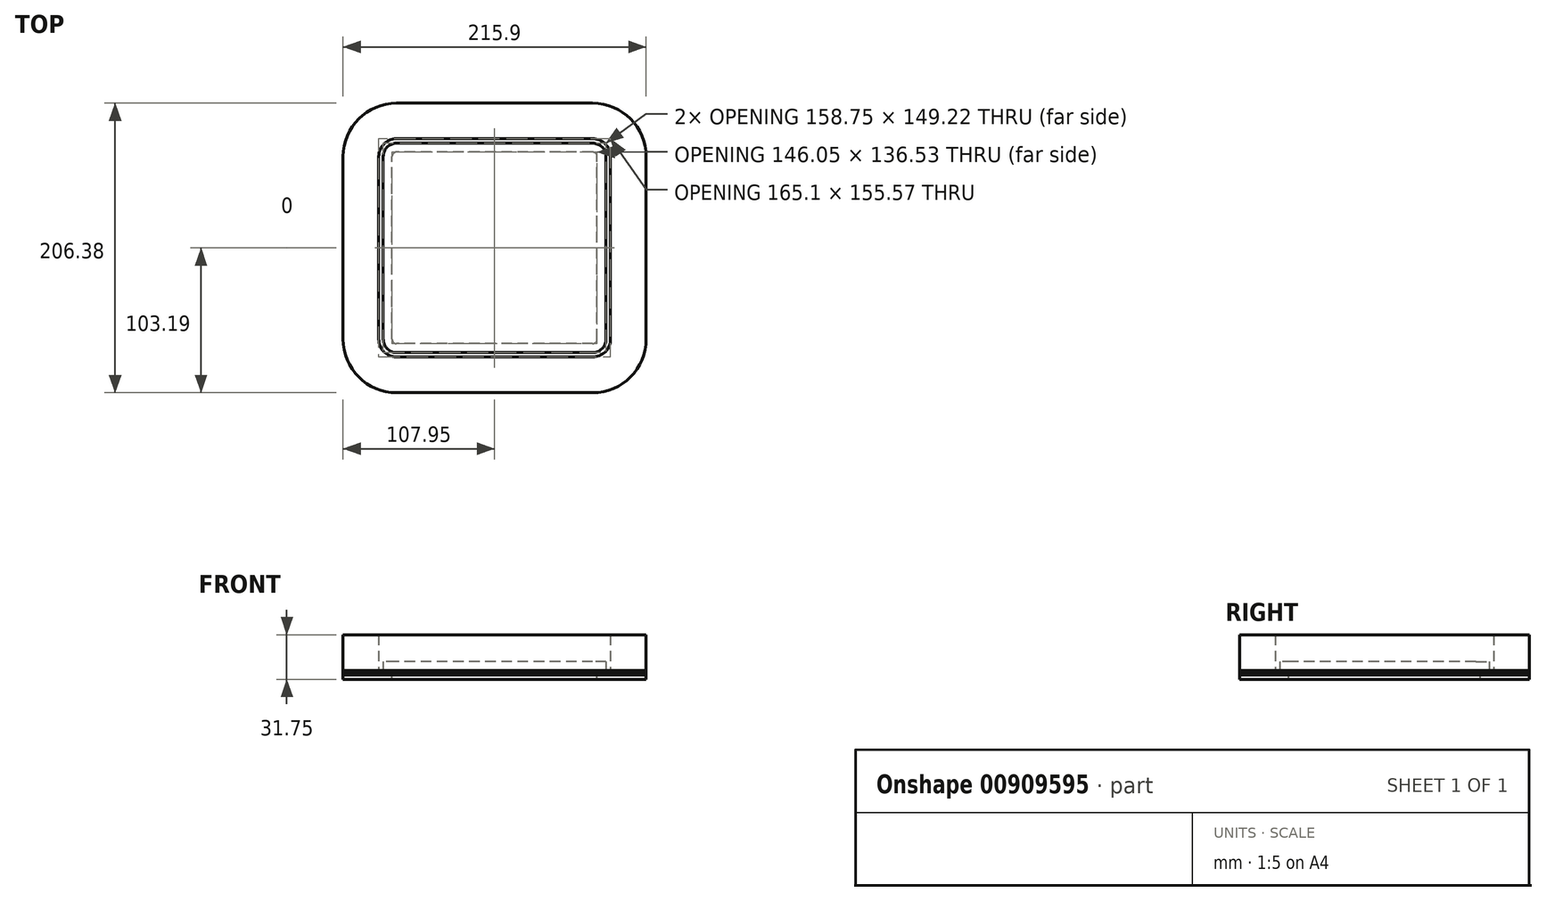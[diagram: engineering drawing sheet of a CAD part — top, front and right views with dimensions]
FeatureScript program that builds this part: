
annotation { "Feature Type Name" : "Feature", "Feature Type Description" : "" }
export const myFeature = defineFeature(function(context is Context, id is Id, definition is map)
    precondition{}
    {
        {
            var Q0;
            Q0=qCreatedBy(makeId("Top.planeOp"),FACE);
            var sketch = newSketch(context, id + "F0", { "sketchPlane" : qUnion([Q0])});
            skLineSegment(sketch, "E0.bottom", {"start": v(69.85, 77.79) * mm, "end": v(-69.85, 77.79) * mm});
            skLineSegment(sketch, "E0.top", {"start": v(69.85, -77.79) * mm, "end": v(-69.85, -77.79) * mm});
            skLineSegment(sketch, "E0.left", {"start": v(82.55, 65.09) * mm, "end": v(82.55, -65.09) * mm});
            skLineSegment(sketch, "E0.right", {"start": v(-82.55, 65.09) * mm, "end": v(-82.55, -65.09) * mm});
            skPoint(sketch, "E0.middle", {"position": v(0, 0) * mm});
            skPoint(sketch, "E1.visualSharp", {"position": v(-82.55, 77.79) * mm});
            skArc(sketch, "E1.filletArc", {"start": v(-69.85, 77.79) * mm, "mid": v(-78.83, 74.07) * mm, "end": v(-82.55, 65.09) * mm});
            skPoint(sketch, "E2.visualSharp", {"position": v(82.55, 77.79) * mm});
            skArc(sketch, "E2.filletArc", {"start": v(82.55, 65.09) * mm, "mid": v(78.83, 74.07) * mm, "end": v(69.85, 77.79) * mm});
            skPoint(sketch, "E3.visualSharp", {"position": v(82.55, -77.79) * mm});
            skArc(sketch, "E3.filletArc", {"start": v(69.85, -77.79) * mm, "mid": v(78.83, -74.07) * mm, "end": v(82.55, -65.09) * mm});
            skPoint(sketch, "E4.visualSharp", {"position": v(-82.55, -77.79) * mm});
            skArc(sketch, "E4.filletArc", {"start": v(-82.55, -65.09) * mm, "mid": v(-78.83, -74.07) * mm, "end": v(-69.85, -77.79) * mm});
            skLineSegment(sketch, "E5.0", {"start": v(-107.95, 65.09) * mm, "end": v(-107.95, -65.09) * mm});
            skArc(sketch, "E5.1", {"start": v(-69.85, 103.19) * mm, "mid": v(-96.8, 92.03) * mm, "end": v(-107.95, 65.09) * mm});
            skArc(sketch, "E5.2", {"start": v(-107.95, -65.09) * mm, "mid": v(-96.8, -92.03) * mm, "end": v(-69.85, -103.19) * mm});
            skLineSegment(sketch, "E5.3", {"start": v(69.85, 103.19) * mm, "end": v(-69.85, 103.19) * mm});
            skLineSegment(sketch, "E5.4", {"start": v(69.85, -103.19) * mm, "end": v(-69.85, -103.19) * mm});
            skArc(sketch, "E5.5", {"start": v(69.85, -103.19) * mm, "mid": v(96.8, -92.03) * mm, "end": v(107.95, -65.09) * mm});
            skLineSegment(sketch, "E5.6", {"start": v(107.95, 65.09) * mm, "end": v(107.95, -65.09) * mm});
            skArc(sketch, "E5.7", {"start": v(107.95, 65.09) * mm, "mid": v(96.8, 92.03) * mm, "end": v(69.85, 103.19) * mm});
            skArc(sketch, "E6.0", {"start": v(79.38, 65.09) * mm, "mid": v(76.59, 71.82) * mm, "end": v(69.85, 74.61) * mm});
            skLineSegment(sketch, "E6.1", {"start": v(69.85, 74.61) * mm, "end": v(-69.85, 74.61) * mm});
            skLineSegment(sketch, "E6.2", {"start": v(79.38, 65.09) * mm, "end": v(79.38, -65.09) * mm});
            skArc(sketch, "E6.3", {"start": v(-69.85, 74.61) * mm, "mid": v(-76.59, 71.82) * mm, "end": v(-79.38, 65.09) * mm});
            skArc(sketch, "E6.4", {"start": v(69.85, -74.61) * mm, "mid": v(76.59, -71.82) * mm, "end": v(79.38, -65.09) * mm});
            skLineSegment(sketch, "E6.5", {"start": v(69.85, -74.61) * mm, "end": v(-69.85, -74.61) * mm});
            skArc(sketch, "E6.6", {"start": v(-79.38, -65.09) * mm, "mid": v(-76.59, -71.82) * mm, "end": v(-69.85, -74.61) * mm});
            skLineSegment(sketch, "E6.7", {"start": v(-79.38, 65.09) * mm, "end": v(-79.38, -65.09) * mm});
            skArc(sketch, "E7.0", {"start": v(69.85, -68.26) * mm, "mid": v(72.1, -67.33) * mm, "end": v(73.03, -65.09) * mm});
            skLineSegment(sketch, "E7.1", {"start": v(73.03, 65.09) * mm, "end": v(73.03, -65.09) * mm});
            skLineSegment(sketch, "E7.2", {"start": v(69.85, -68.26) * mm, "end": v(-69.85, -68.26) * mm});
            skArc(sketch, "E7.3", {"start": v(73.03, 65.09) * mm, "mid": v(72.1, 67.33) * mm, "end": v(69.85, 68.26) * mm});
            skArc(sketch, "E7.4", {"start": v(-73.03, -65.09) * mm, "mid": v(-72.1, -67.33) * mm, "end": v(-69.85, -68.26) * mm});
            skLineSegment(sketch, "E7.5", {"start": v(-73.02, 65.09) * mm, "end": v(-73.03, -65.09) * mm});
            skArc(sketch, "E7.6", {"start": v(-69.85, 68.26) * mm, "mid": v(-72.1, 67.33) * mm, "end": v(-73.02, 65.09) * mm});
            skLineSegment(sketch, "E7.7", {"start": v(69.85, 68.26) * mm, "end": v(-69.85, 68.26) * mm});
            skSolve(sketch);
        }
        {
            var Q0;
            Q0=makeQuery(id+"F0.imprint","IMPRINT",FACE,{"disambiguationData":[TD([[makeQuery(id+"F0.imprint","IMPRINT",EDGE,{"derivedFrom":sQuery(id+"F0.wireOp",EDGE,"E0.bottom")}),-1.0]])]});
            extrude(context, id + "F1", {"entities" : qUnion([Q0]), "depth" : 25.4 * mm, "offsetDistance" : 25.4 * mm});
        }
        {
            var Q0;
            Q0=makeQuery(id+"F0.imprint","IMPRINT",FACE,{"disambiguationData":[TD([[makeQuery(id+"F0.imprint","IMPRINT",EDGE,{"derivedFrom":sQuery(id+"F0.wireOp",EDGE,"E6.0")}),1.0]])]});
            var Q1;
            Q1=makeQuery(id+"F0.imprint","IMPRINT",FACE,{"disambiguationData":[TD([[makeQuery(id+"F0.imprint","IMPRINT",EDGE,{"derivedFrom":sQuery(id+"F0.wireOp",EDGE,"E7.0")}),1.0]])]});
            extrude(context, id + "F2", {"entities" : qUnion([Q0, Q1]), "depth" : 6.35 * mm, "offsetDistance" : 25.4 * mm});
        }
        {
            var Q0;
            Q0=makeQuery(id+"F0.imprint","IMPRINT",FACE,{"disambiguationData":[TD([[makeQuery(id+"F0.imprint","IMPRINT",EDGE,{"derivedFrom":sQuery(id+"F0.wireOp",EDGE,"E0.bottom")}),-1.0]])]});
            var Q1;
            Q1=makeQuery(id+"F0.imprint","IMPRINT",FACE,{"disambiguationData":[TD([[makeQuery(id+"F0.imprint","IMPRINT",EDGE,{"derivedFrom":sQuery(id+"F0.wireOp",EDGE,"E0.bottom")}),1.0]])]});
            extrude(context, id + "F3", {"entities" : qUnion([Q0, Q1]), "oppositeDirection" : true, "depth" : 1.59 * mm, "offsetDistance" : 25.4 * mm});
        }
        {
            var Q0;
            Q0=makeQuery(id+"F3.opExtrude","CAP_FACE",FACE,{"disambiguationData":[OSD([sQuery(id+"F0.wireOp",EDGE,"E5.0"),sQuery(id+"F0.wireOp",EDGE,"E5.1"),sQuery(id+"F0.wireOp",EDGE,"E5.2"),sQuery(id+"F0.wireOp",EDGE,"E5.3"),sQuery(id+"F0.wireOp",EDGE,"E5.4"),sQuery(id+"F0.wireOp",EDGE,"E5.5"),sQuery(id+"F0.wireOp",EDGE,"E5.6"),sQuery(id+"F0.wireOp",EDGE,"E5.7"),sQuery(id+"F0.wireOp",EDGE,"E7.0"),sQuery(id+"F0.wireOp",EDGE,"E7.1"),sQuery(id+"F0.wireOp",EDGE,"E7.2"),sQuery(id+"F0.wireOp",EDGE,"E7.3"),sQuery(id+"F0.wireOp",EDGE,"E7.4"),sQuery(id+"F0.wireOp",EDGE,"E7.5"),sQuery(id+"F0.wireOp",EDGE,"E7.6"),sQuery(id+"F0.wireOp",EDGE,"E7.7")])],"isStart":false});
            extrude(context, id + "F4", {"entities" : qUnion([Q0]), "depth" : 1.59 * mm, "offsetDistance" : 25.4 * mm});
        }
        {
            var Q0;
            Q0=makeQuery(id+"F4.opExtrude","CAP_FACE",FACE,{"disambiguationData":[OSD([sQuery(id+"F0.wireOp",EDGE,"E5.0"),sQuery(id+"F0.wireOp",EDGE,"E5.1"),sQuery(id+"F0.wireOp",EDGE,"E5.2"),sQuery(id+"F0.wireOp",EDGE,"E5.3"),sQuery(id+"F0.wireOp",EDGE,"E5.4"),sQuery(id+"F0.wireOp",EDGE,"E5.5"),sQuery(id+"F0.wireOp",EDGE,"E5.6"),sQuery(id+"F0.wireOp",EDGE,"E5.7"),sQuery(id+"F0.wireOp",EDGE,"E6.0"),sQuery(id+"F0.wireOp",EDGE,"E6.1"),sQuery(id+"F0.wireOp",EDGE,"E6.2"),sQuery(id+"F0.wireOp",EDGE,"E6.3"),sQuery(id+"F0.wireOp",EDGE,"E6.4"),sQuery(id+"F0.wireOp",EDGE,"E6.5"),sQuery(id+"F0.wireOp",EDGE,"E6.6"),sQuery(id+"F0.wireOp",EDGE,"E6.7")])],"isStart":false});
            var sketch = newSketch(context, id + "F5", { "sketchPlane" : qUnion([Q0])});
            skLineSegment(sketch, "E8.bottom", {"start": v(69.85, 77.79) * mm, "end": v(-69.85, 77.79) * mm});
            skLineSegment(sketch, "E8.top", {"start": v(69.85, -77.79) * mm, "end": v(-69.85, -77.79) * mm});
            skLineSegment(sketch, "E8.left", {"start": v(82.55, 65.09) * mm, "end": v(82.55, -65.09) * mm});
            skLineSegment(sketch, "E8.right", {"start": v(-82.55, 65.09) * mm, "end": v(-82.55, -65.09) * mm});
            skPoint(sketch, "E8.middle", {"position": v(0, 0) * mm});
            skPoint(sketch, "E9.visualSharp", {"position": v(-82.55, 77.79) * mm});
            skArc(sketch, "E9.filletArc", {"start": v(-69.85, 77.79) * mm, "mid": v(-78.83, 74.07) * mm, "end": v(-82.55, 65.09) * mm});
            skPoint(sketch, "E10.visualSharp", {"position": v(82.55, 77.79) * mm});
            skArc(sketch, "E10.filletArc", {"start": v(82.55, 65.09) * mm, "mid": v(78.83, 74.07) * mm, "end": v(69.85, 77.79) * mm});
            skPoint(sketch, "E11.visualSharp", {"position": v(82.55, -77.79) * mm});
            skArc(sketch, "E11.filletArc", {"start": v(69.85, -77.79) * mm, "mid": v(78.83, -74.07) * mm, "end": v(82.55, -65.09) * mm});
            skPoint(sketch, "E12.visualSharp", {"position": v(-82.55, -77.79) * mm});
            skArc(sketch, "E12.filletArc", {"start": v(-82.55, -65.09) * mm, "mid": v(-78.83, -74.07) * mm, "end": v(-69.85, -77.79) * mm});
            skLineSegment(sketch, "E13.0", {"start": v(-107.95, 65.09) * mm, "end": v(-107.95, -65.09) * mm});
            skArc(sketch, "E13.1", {"start": v(-69.85, 103.19) * mm, "mid": v(-96.8, 92.03) * mm, "end": v(-107.95, 65.09) * mm});
            skArc(sketch, "E13.2", {"start": v(-107.95, -65.09) * mm, "mid": v(-96.8, -92.03) * mm, "end": v(-69.85, -103.19) * mm});
            skLineSegment(sketch, "E13.3", {"start": v(69.85, 103.19) * mm, "end": v(-69.85, 103.19) * mm});
            skLineSegment(sketch, "E13.4", {"start": v(69.85, -103.19) * mm, "end": v(-69.85, -103.19) * mm});
            skArc(sketch, "E13.5", {"start": v(69.85, -103.19) * mm, "mid": v(96.8, -92.03) * mm, "end": v(107.95, -65.09) * mm});
            skLineSegment(sketch, "E13.6", {"start": v(107.95, 65.09) * mm, "end": v(107.95, -65.09) * mm});
            skArc(sketch, "E13.7", {"start": v(107.95, 65.09) * mm, "mid": v(96.8, 92.03) * mm, "end": v(69.85, 103.19) * mm});
            skArc(sketch, "E14.0", {"start": v(79.38, 65.09) * mm, "mid": v(76.59, 71.82) * mm, "end": v(69.85, 74.61) * mm});
            skLineSegment(sketch, "E14.1", {"start": v(69.85, 74.61) * mm, "end": v(-69.85, 74.61) * mm});
            skLineSegment(sketch, "E14.2", {"start": v(79.38, 65.09) * mm, "end": v(79.38, -65.09) * mm});
            skArc(sketch, "E14.3", {"start": v(-69.85, 74.61) * mm, "mid": v(-76.59, 71.82) * mm, "end": v(-79.38, 65.09) * mm});
            skArc(sketch, "E14.4", {"start": v(69.85, -74.61) * mm, "mid": v(76.59, -71.82) * mm, "end": v(79.38, -65.09) * mm});
            skLineSegment(sketch, "E14.5", {"start": v(69.85, -74.61) * mm, "end": v(-69.85, -74.61) * mm});
            skArc(sketch, "E14.6", {"start": v(-79.38, -65.09) * mm, "mid": v(-76.59, -71.82) * mm, "end": v(-69.85, -74.61) * mm});
            skLineSegment(sketch, "E14.7", {"start": v(-79.37, 65.09) * mm, "end": v(-79.38, -65.09) * mm});
            skArc(sketch, "E15.0", {"start": v(69.85, -68.26) * mm, "mid": v(72.1, -67.33) * mm, "end": v(73.03, -65.09) * mm});
            skLineSegment(sketch, "E15.1", {"start": v(73.03, 65.09) * mm, "end": v(73.03, -65.09) * mm});
            skLineSegment(sketch, "E15.2", {"start": v(69.85, -68.26) * mm, "end": v(-69.85, -68.26) * mm});
            skArc(sketch, "E15.3", {"start": v(73.03, 65.09) * mm, "mid": v(72.1, 67.33) * mm, "end": v(69.85, 68.26) * mm});
            skArc(sketch, "E15.4", {"start": v(-73.03, -65.09) * mm, "mid": v(-72.1, -67.33) * mm, "end": v(-69.85, -68.26) * mm});
            skLineSegment(sketch, "E15.5", {"start": v(-73.02, 65.09) * mm, "end": v(-73.03, -65.09) * mm});
            skArc(sketch, "E15.6", {"start": v(-69.85, 68.26) * mm, "mid": v(-72.1, 67.33) * mm, "end": v(-73.02, 65.09) * mm});
            skLineSegment(sketch, "E15.7", {"start": v(69.85, 68.26) * mm, "end": v(-69.85, 68.26) * mm});
            skSolve(sketch);
        }
        {
            var Q0;
            Q0=makeQuery(id+"F5.imprint","IMPRINT",FACE,{"disambiguationData":[TD([[makeQuery(id+"F5.imprint","IMPRINT",EDGE,{"derivedFrom":sQuery(id+"F5.wireOp",EDGE,"E8.bottom")}),-1.0]])]});
            var Q1;
            Q1=makeQuery(id+"F5.imprint","IMPRINT",FACE,{"disambiguationData":[TD([[makeQuery(id+"F5.imprint","IMPRINT",EDGE,{"derivedFrom":sQuery(id+"F5.wireOp",EDGE,"E14.0")}),-1.0]])]});
            var Q2;
            Q2=makeQuery(id+"F5.imprint","IMPRINT",FACE,{"disambiguationData":[TD([[makeQuery(id+"F5.imprint","IMPRINT",EDGE,{"derivedFrom":sQuery(id+"F5.wireOp",EDGE,"E8.bottom")}),1.0]])]});
            extrude(context, id + "F6", {"entities" : qUnion([Q0, Q1, Q2]), "depth" : 3.17 * mm, "offsetDistance" : 25.4 * mm});
        }
    });
